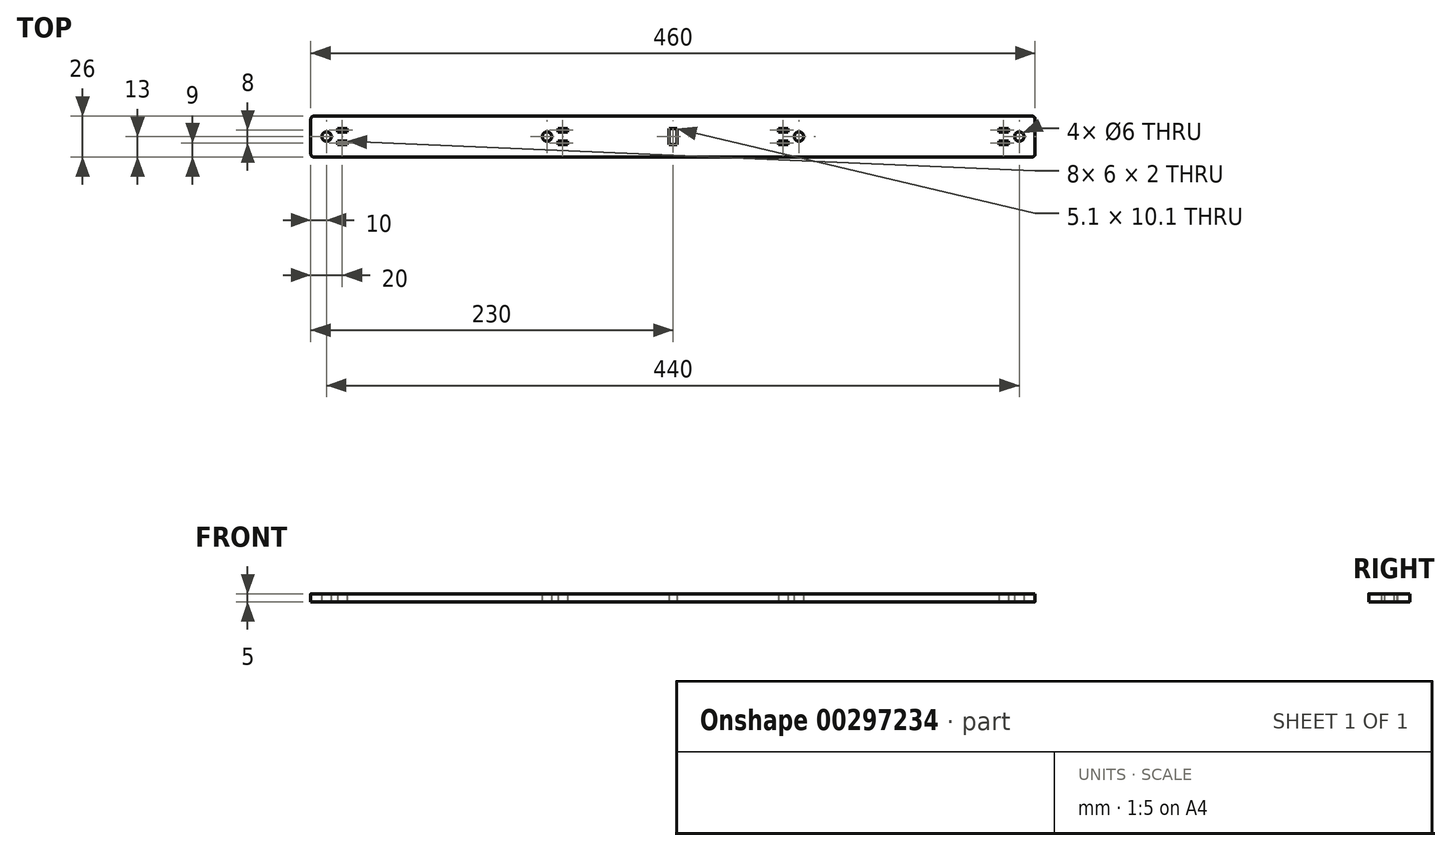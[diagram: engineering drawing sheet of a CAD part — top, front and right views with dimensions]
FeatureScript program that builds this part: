
annotation { "Feature Type Name" : "Feature", "Feature Type Description" : "" }
export const myFeature = defineFeature(function(context is Context, id is Id, definition is map)
    precondition{}
    {
        {
            var Q0;
            Q0=qCreatedBy(makeId("Top.planeOp"),FACE);
            var sketch = newSketch(context, id + "F0", { "sketchPlane" : qUnion([Q0])});
            skCircle(sketch, "E0", {"center": v(-70, 0) * mm, "radius": 3 * mm});
            skCircle(sketch, "E1.MirrorC", {"center": v(70, 0) * mm, "radius": 3 * mm});
            skCircle(sketch, "E2", {"center": v(230, 0) * mm, "radius": 3 * mm});
            skCircle(sketch, "E3.MirrorC", {"center": v(370, 0) * mm, "radius": 3 * mm});
            skPoint(sketch, "E4", {"position": v(150, 0) * mm});
            skLineSegment(sketch, "E5.bottom", {"start": v(-78, -13) * mm, "end": v(378, -13) * mm});
            skLineSegment(sketch, "E5.top", {"start": v(-78, 13) * mm, "end": v(378, 13) * mm});
            skLineSegment(sketch, "E5.left", {"start": v(-80, -11) * mm, "end": v(-80, 11) * mm});
            skLineSegment(sketch, "E5.right", {"start": v(380, -11) * mm, "end": v(380, 11) * mm});
            skLineSegment(sketch, "E6.bottom", {"start": v(152.55, -5.05) * mm, "end": v(147.45, -5.05) * mm});
            skLineSegment(sketch, "E6.top", {"start": v(152.55, 5.05) * mm, "end": v(147.45, 5.05) * mm});
            skLineSegment(sketch, "E6.left", {"start": v(152.55, -5.05) * mm, "end": v(152.55, 5.05) * mm});
            skLineSegment(sketch, "E6.right", {"start": v(147.45, -5.05) * mm, "end": v(147.45, 5.05) * mm});
            skPoint(sketch, "E7.visualSharp", {"position": v(-80, 13) * mm});
            skArc(sketch, "E7.filletArc", {"start": v(-78, 13) * mm, "mid": v(-79.41, 12.41) * mm, "end": v(-80, 11) * mm});
            skPoint(sketch, "E8.visualSharp", {"position": v(-80, -13) * mm});
            skArc(sketch, "E8.filletArc", {"start": v(-80, -11) * mm, "mid": v(-79.41, -12.41) * mm, "end": v(-78, -13) * mm});
            skPoint(sketch, "E9.visualSharp", {"position": v(380, 13) * mm});
            skArc(sketch, "E9.filletArc", {"start": v(380, 11) * mm, "mid": v(379.41, 12.41) * mm, "end": v(378, 13) * mm});
            skPoint(sketch, "E10.visualSharp", {"position": v(380, -13) * mm});
            skArc(sketch, "E10.filletArc", {"start": v(378, -13) * mm, "mid": v(379.41, -12.41) * mm, "end": v(380, -11) * mm});
            skLineSegment(sketch, "E11.bottom", {"start": v(-63, 5) * mm, "end": v(-57, 5) * mm});
            skLineSegment(sketch, "E11.top", {"start": v(-63, 3) * mm, "end": v(-57, 3) * mm});
            skLineSegment(sketch, "E11.left", {"start": v(-63, 5) * mm, "end": v(-63, 3) * mm});
            skLineSegment(sketch, "E11.right", {"start": v(-57, 5) * mm, "end": v(-57, 3) * mm});
            skLineSegment(sketch, "E12.bottom", {"start": v(-63, -3) * mm, "end": v(-57, -3) * mm});
            skLineSegment(sketch, "E12.top", {"start": v(-63, -5) * mm, "end": v(-57, -5) * mm});
            skLineSegment(sketch, "E12.left", {"start": v(-63, -3) * mm, "end": v(-63, -5) * mm});
            skLineSegment(sketch, "E12.right", {"start": v(-57, -3) * mm, "end": v(-57, -5) * mm});
            skPoint(sketch, "E13", {"position": v(-50, 0) * mm});
            skLineSegment(sketch, "E14.bottom", {"start": v(77, 5) * mm, "end": v(83, 5) * mm});
            skLineSegment(sketch, "E14.top", {"start": v(77, 3) * mm, "end": v(83, 3) * mm});
            skLineSegment(sketch, "E14.left", {"start": v(77, 5) * mm, "end": v(77, 3) * mm});
            skLineSegment(sketch, "E14.right", {"start": v(83, 5) * mm, "end": v(83, 3) * mm});
            skLineSegment(sketch, "E15.bottom", {"start": v(77, -3) * mm, "end": v(83, -3) * mm});
            skLineSegment(sketch, "E15.top", {"start": v(77, -5) * mm, "end": v(83, -5) * mm});
            skLineSegment(sketch, "E15.left", {"start": v(77, -3) * mm, "end": v(77, -5) * mm});
            skLineSegment(sketch, "E15.right", {"start": v(83, -3) * mm, "end": v(83, -5) * mm});
            skPoint(sketch, "E16", {"position": v(90, 0) * mm});
            skPoint(sketch, "E17", {"position": v(210, 0) * mm});
            skLineSegment(sketch, "E18.bottom", {"start": v(217, 5) * mm, "end": v(223, 5) * mm});
            skLineSegment(sketch, "E18.top", {"start": v(217, 3) * mm, "end": v(223, 3) * mm});
            skLineSegment(sketch, "E18.left", {"start": v(217, 5) * mm, "end": v(217, 3) * mm});
            skLineSegment(sketch, "E18.right", {"start": v(223, 5) * mm, "end": v(223, 3) * mm});
            skLineSegment(sketch, "E19.bottom", {"start": v(217, -3) * mm, "end": v(223, -3) * mm});
            skLineSegment(sketch, "E19.top", {"start": v(217, -5) * mm, "end": v(223, -5) * mm});
            skLineSegment(sketch, "E19.left", {"start": v(217, -3) * mm, "end": v(217, -5) * mm});
            skLineSegment(sketch, "E19.right", {"start": v(223, -3) * mm, "end": v(223, -5) * mm});
            skPoint(sketch, "E20", {"position": v(350, 0) * mm});
            skLineSegment(sketch, "E21.bottom", {"start": v(357, 5) * mm, "end": v(363, 5) * mm});
            skLineSegment(sketch, "E21.top", {"start": v(357, 3) * mm, "end": v(363, 3) * mm});
            skLineSegment(sketch, "E21.left", {"start": v(357, 5) * mm, "end": v(357, 3) * mm});
            skLineSegment(sketch, "E21.right", {"start": v(363, 5) * mm, "end": v(363, 3) * mm});
            skLineSegment(sketch, "E22.bottom", {"start": v(357, -3) * mm, "end": v(363, -3) * mm});
            skLineSegment(sketch, "E22.top", {"start": v(357, -5) * mm, "end": v(363, -5) * mm});
            skLineSegment(sketch, "E22.left", {"start": v(357, -3) * mm, "end": v(357, -5) * mm});
            skLineSegment(sketch, "E22.right", {"start": v(363, -3) * mm, "end": v(363, -5) * mm});
            skSolve(sketch);
        }
        {
            var Q0;
            Q0=makeQuery(id+"F0.imprint","IMPRINT",FACE,{"disambiguationData":[TD([[makeQuery(id+"F0.imprint","IMPRINT",EDGE,{"derivedFrom":sQuery(id+"F0.wireOp",EDGE,"E0")}),-1.0]])]});
            extrude(context, id + "F1", {"entities" : qUnion([Q0]), "depth" : 5 * mm});
        }
    });
